# Revit family: Shower_System-GROHE-Euphoria_SmartControl-26512000
name_source: partatom
category: Plumbing Fixtures
revit_build: Autodesk Revit 2014 (Build: 20130308_1515(x64)
units: mm (PartAtom-declared; Revit-internal decimal feet)

## types (1)
- 26512000
    Assembly Code = D2010710
    CW Connection = Yes
    CWFU = 3
    Cold Water Connection Diameter = 1/2"
    Cold Water Connection Radius = 1/4"
    Default Elevation = 44"
    Description = Euphoria SmartControl System Duo Shower System with Bath Thermostat for Wall Mount
    Finish = Metal-Grohe-003-Chrome
    Flow Rate = Minimum 1.8 gpm (7 L/min.)
    HW Connection = Yes
    HWFU = 3
    Height = 61 1/16"
    Hot Water Connection Diameter = 1"
    Hot Water Connection Radius = 1/4"
    Installation Type = Wall Mounted
    Length = 17 11/16"
    Manufacturer = Grohe
    Material = Metal-Grohe-003-Chrome
    Model = 26512000
    Price = Prices may vary. Please consult Manufacturer Representative for most up-to-date price list.
    Product Page URL = https://www.grohe.us
    Tempered Connection Diameter = 1/2"
    Tempered Connection Radius = 1/4"
    URL = https://www.grohe.us
    Vent Connection = No
    WFU = 4
    Warranty Documentation Link = https://cdn.cloud.grohe.com
    Waste Connection = No
    Width = 12 1/16"
    cUPC Compliant = Yes

## geometry (parser evidence)
native form markers: Sweep x1
no freeform markers — native parametric forms only
